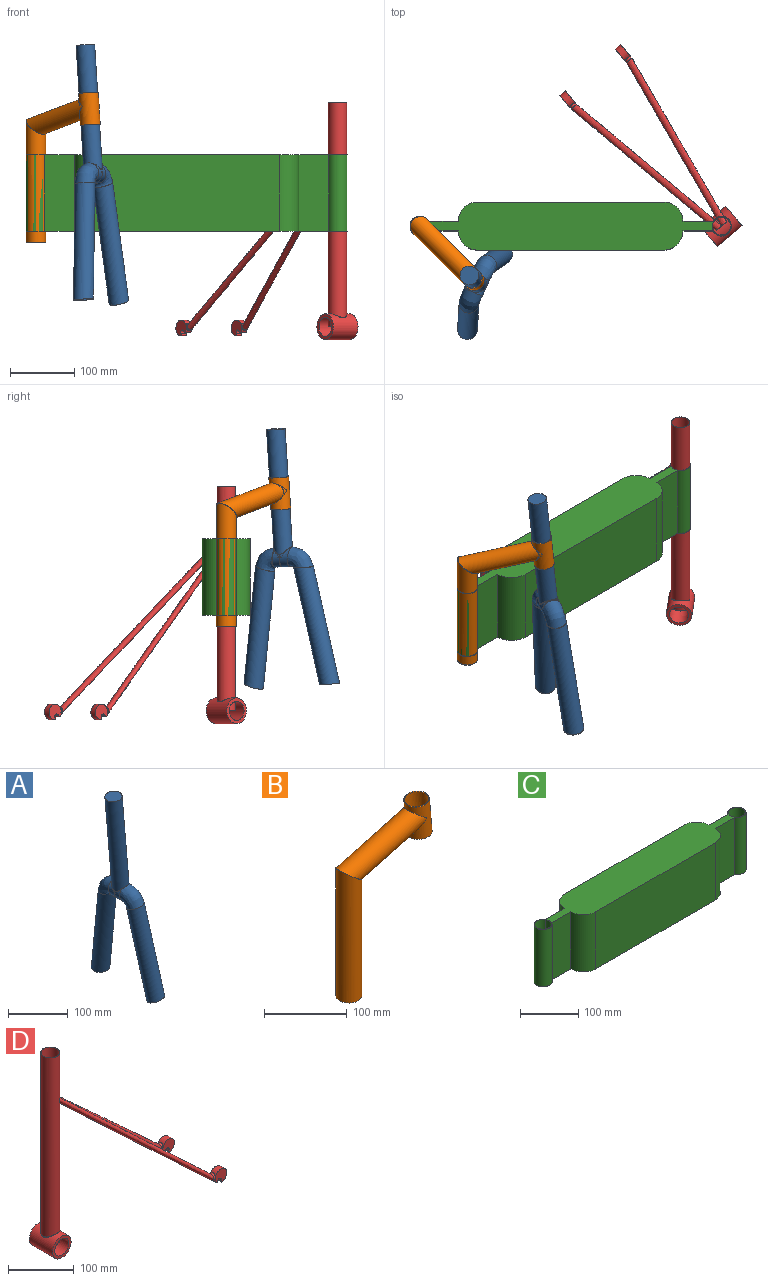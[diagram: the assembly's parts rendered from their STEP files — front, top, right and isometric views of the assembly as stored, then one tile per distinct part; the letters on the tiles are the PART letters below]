
ASSEMBLY  parts=4 mates=3
PART A: 19 faces, bbox 87.7x212.7x433.7 mm
  f0: cylinder r=14.5mm len=28.89mm, axis (-0.09,0,1), area 0mm2, adj f1,f18
  f1: bspline ~28.92x28.2mm, area 851.7mm2, adj f0,f2,f17
  f2: bspline ~36.56x32mm, area 2543mm2, adj f1,f3
  f3: bspline ~185.29x61.09mm, area 16876.9mm2, adj f2,f4
  f4: plane 35.31x35.2mm, normal (0.09,0,-1), area 94.2mm2, adj f3,f5
  f5: bspline ~185.48x94.35mm, area 18040.8mm2, adj f4,f6
  f6: bspline ~63.76x63.53mm, area 2722.3mm2, adj f5,f7
  f7: bspline ~30.91x30.14mm, area 968.2mm2, adj f6,f8,f16
  f8: cylinder r=14.5mm len=196.39mm, axis (-0.09,0,1), area 17224.1mm2, adj f7,f9,f10,f16
  f9: plane 29x28.89mm, normal (-0.09,0,1), area 660.5mm2, adj f8
  f10: bspline ~68.97x58.26mm, area 2722.3mm2, adj f8,f11,f16
  f11: bspline ~206.6x90.61mm, area 18040.8mm2, adj f10,f12
  f12: plane 35.21x33.44mm, normal (0.08,-0.34,-0.94), area 94.2mm2, adj f11,f13
  f13: bspline ~192.89x59.36mm, area 16876.9mm2, adj f12,f14
  f14: bspline ~35.78x35.7mm, area 2543mm2, adj f13,f15,f17
  f15: cylinder r=14.5mm len=29.86mm, axis (-0.09,0,1), area 362.2mm2, adj f14,f17,f18
  f16: bspline ~30.88x28.07mm, area 862.9mm2, adj f7,f8,f10
  f17: bspline ~28.89x26.01mm, area 749.8mm2, adj f1,f14,f15
  f18: plane 51.05x50.94mm, normal (0.09,0,-1), area 660.5mm2, adj f0,f15
PART B: 10 faces, bbox 150.8x31x233.5 mm
  f0: cylinder r=14.5mm len=130.33mm, axis (0.97,0,0.26), area 10043.3mm2, adj f1,f8
  f1: cylinder r=14.5mm len=191.13mm, axis (0,0,1), area 16399.1mm2, adj f0,f2
  f2: plane 31x31mm, normal (0,0,-1), area 94.2mm2, adj f1,f4
  f3: cylinder r=15.5mm len=136.87mm, axis (0.97,0,0.26), area 10857mm2, adj f4,f6
  f4: cylinder r=15.5mm len=191.89mm, axis (0,0,1), area 17530.1mm2, adj f2,f3
  f5: plane 31x30.88mm, normal (0.09,0,-1), area 94.2mm2, adj f6,f9
  f6: cylinder r=15.5mm len=52.51mm, axis (-0.09,0,1), area 3893.6mm2, adj f3,f5,f7
  f7: plane 31x30.88mm, normal (-0.09,0,1), area 94.2mm2, adj f6,f9
  f8: cylinder r=15.5mm len=30.21mm, axis (-0.09,0,1), area 797.5mm2, adj f0
  f9: cylinder r=14.5mm len=52.34mm, axis (-0.09,0,1), area 4555.3mm2, adj f5,f7
PART C: 16 faces, bbox 501x75x120 mm
  f0: plane 120x46.44mm, normal (0,1,0), area 5572.2mm2, adj f1,f10,f11,f15
  f1: cylinder r=15.5mm len=120mm, axis (0,0,-1), area 9807.9mm2, adj f0,f2,f10,f11
  f2: plane 120x46.44mm, normal (0,-1,0), area 5572.2mm2, adj f1,f10,f11,f12
  f3: plane 290x120mm, normal (0,-1,0), area 34800mm2, adj f10,f11,f12,f13
  f4: plane 120x46.44mm, normal (0,-1,0), area 5572.2mm2, adj f5,f10,f11,f13
  f5: cylinder r=15.5mm len=120mm, axis (0,0,-1), area 9807.9mm2, adj f4,f6,f10,f11
  f6: plane 120x46.44mm, normal (0,1,0), area 5572.2mm2, adj f5,f10,f11,f14
  f7: cylinder r=14.5mm len=120mm, axis (0,0,-1), area 10932.7mm2, adj f10,f11
  f8: plane 290x120mm, normal (0,1,0), area 34800mm2, adj f10,f11,f14,f15
  f9: cylinder r=14.5mm len=120mm, axis (0,0,-1), area 10932.7mm2, adj f10,f11
  f10: plane 501x75mm, normal (0,0,1), area 27019.8mm2, adj f0,f1,f2,f3,f4,f5,f6,f7
  f11: plane 501x75mm, normal (0,0,-1), area 27019.8mm2, adj f0,f1,f2,f3,f4,f5,f6,f7
  f12: cylinder r=30mm len=120mm, axis (0,0,-1), area 5654.9mm2, adj f2,f3,f10,f11
  f13: cylinder r=30mm len=120mm, axis (0,0,1), area 5654.9mm2, adj f3,f4,f10,f11
  f14: cylinder r=30mm len=120mm, axis (0,0,-1), area 5654.9mm2, adj f6,f8,f10,f11
  f15: cylinder r=30mm len=120mm, axis (0,0,1), area 5654.9mm2, adj f0,f8,f10,f11
PART D: 45 faces, bbox 340.2x125.6x372.1 mm
  f0: cylinder r=5.5mm len=11mm, axis (-1,0,0), area 113.9mm2, adj f31,f32,f33
  f1: bspline ~290.64x281mm, area 3.1mm2, adj f15,f27
  f2: cylinder r=15mm len=50mm, axis (0,1,0), area 3966.7mm2, adj f4,f5,f11
  f3: cylinder r=20mm len=50mm, axis (0,1,0), area 5628.8mm2, adj f4,f5,f6
  f4: plane 40x40mm, normal (0,-1,0), area 549.8mm2, adj f2,f3
  f5: plane 40x40mm, normal (0,1,0), area 549.8mm2, adj f2,f3
  f6: cylinder r=14.5mm len=336.23mm, axis (0,0,-1), area 30143.3mm2, adj f3,f7,f18,f31
  f7: plane 29x29mm, normal (0,0,1), area 44.8mm2, adj f6,f8
  f8: cylinder r=14mm len=335.72mm, axis (0,0,-1), area 29073.1mm2, adj f7,f9,f16,f28
  f9: cylinder r=20mm len=28mm, axis (0,1,0), area 605.8mm2, adj f8
  f10: plane 29x29mm, normal (0,0,-1), area 44.8mm2, adj f11,f12
  f11: cylinder r=14.5mm len=29mm, axis (0,0,-1), area 916.1mm2, adj f2,f10
  f12: cylinder r=14mm len=28mm, axis (0,0,-1), area 934.3mm2, adj f10,f13
  f13: cylinder r=15mm len=28mm, axis (0,1,0), area 672.8mm2, adj f12
  f14: bspline ~22.76x13.79mm, area 434.7mm2, adj f15,f17,f29
  f15: plane 23.08x13.08mm, normal (-1,0,0), area 32mm2, adj f1,f14,f16,f27,f28,f29
  f16: bspline ~23.82x13.86mm, area 464.3mm2, adj f8,f15,f28
  f17: cylinder r=14mm len=11.32mm, axis (0,0,-1), area 84.9mm2, adj f14
  f18: bspline ~282.43x273.31mm, area 11538.3mm2, adj f6,f19
  f19: cylinder r=5.5mm len=11mm, axis (-1,0,0), area 113.9mm2, adj f18,f20,f21
  f20: cylinder r=12.5mm len=11mm, axis (0,1,0), area 50mm2, adj f19,f24,f25,f26
  f21: cylinder r=12.5mm len=24.84mm, axis (0,1,0), area 550.2mm2, adj f19,f22,f25,f26
  f22: cylinder r=2mm len=11mm, axis (0,1,0), area 51.4mm2, adj f21,f23,f25,f26
  f23: cylinder r=4mm len=11mm, axis (0,1,0), area 153mm2, adj f22,f24,f25,f26
  f24: cylinder r=2mm len=11mm, axis (0,1,0), area 51.4mm2, adj f20,f23,f25,f26
  f25: plane 25x24.84mm, normal (0,-1,0), area 424.3mm2, adj f20,f21,f22,f23,f24
  f26: plane 25x24.84mm, normal (0,1,0), area 424.3mm2, adj f20,f21,f22,f23,f24
  f27: bspline ~22.76x13.79mm, area 434.6mm2, adj f1,f15,f30
  f28: bspline ~23.82x13.86mm, area 464.2mm2, adj f8,f15,f16
  f29: bspline ~290.64x281mm, area 3.1mm2, adj f14,f15
  f30: cylinder r=14mm len=11.32mm, axis (0,0,-1), area 84.9mm2, adj f27
  f31: bspline ~282.43x273.31mm, area 11538.4mm2, adj f0,f6
  f32: cylinder r=12.5mm len=11mm, axis (0,-1,0), area 50mm2, adj f0,f34,f37,f38
  f33: cylinder r=12.5mm len=24.84mm, axis (0,-1,0), area 550.2mm2, adj f0,f36,f37,f38
  f34: cylinder r=2mm len=11mm, axis (0,-1,0), area 51.4mm2, adj f32,f35,f37,f38
  f35: cylinder r=4mm len=11mm, axis (0,-1,0), area 153mm2, adj f34,f36,f37,f38
  f36: cylinder r=2mm len=11mm, axis (0,-1,0), area 51.4mm2, adj f33,f35,f37,f38
  f37: plane 25x24.84mm, normal (0,1,0), area 424.3mm2, adj f32,f33,f34,f35,f36
  f38: plane 25x24.84mm, normal (0,-1,0), area 424.3mm2, adj f32,f33,f34,f35,f36
  f39: plane 11.39x11.39mm, normal (-1,0,0), area 78.5mm2, adj f41
  f40: cylinder r=14.5mm len=11.24mm, axis (0,0,-1), area 84.3mm2, adj f41
  f41: bspline ~278.07x268.27mm, area 10467.4mm2, adj f39,f40
  f42: cylinder r=14.5mm len=11.24mm, axis (0,0,-1), area 84.2mm2, adj f43
  f43: bspline ~278.07x268.27mm, area 10467.4mm2, adj f42,f44
  f44: plane 11.39x11.39mm, normal (-1,0,0), area 78.5mm2, adj f43
PLACE A rot(axis=(-0.08,0.03,1),155.2deg) t=(-24.74,-150.65,31.26)mm
PLACE B rot(axis=(0,0,-1),45deg) t=(-240.86,0,-16.52)mm
PLACE C t=(-5.86,0,0)mm fixed
PLACE D rot(axis=(0,0,1),130deg) t=(229.14,0,-148.52)mm
MATE revolute A.f0 <-> B.f9  axis (-0.06,0.06,1) through (-163.78,-77.08,290.37)mm
MATE revolute D.f6 <-> C.f5  axis (0,0,-1) through (229.14,0,110)mm
MATE revolute C.f1 <-> B.f4  axis (0,0,-1) through (-240.86,0,60)mm
